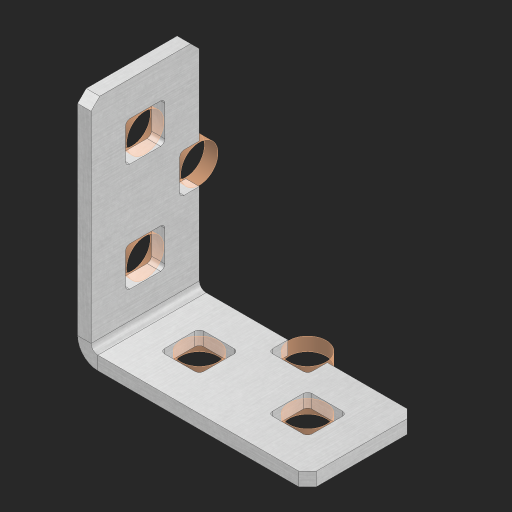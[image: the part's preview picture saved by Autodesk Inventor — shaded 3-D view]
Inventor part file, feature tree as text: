
AUTODESK INVENTOR PART (.ipt)
format: ipt  version: 2023 (Build 270158000, 158)  size: 512,512 bytes
history: native  units: in
note: dims shown in document units (in); Inventor stores cm internally (conversion verified against a paired STEP export)
features: other x78, extrude x70, sheet_metal_op x8, sketch x7, pattern_linear x2, mirror x1, chamfer x1
ambient origin geometry x8: Origin, YZ Plane, XZ Plane, XY Plane, X Axis, Y Axis, Z Axis, Center Point
bodies: Solid1 (feature_tree), Body (feature_tree)
feature tree (167):
  sheet_metal_op  "Flanges"
  sheet_metal_op  "Body Pattern"
  pattern_linear  "Center Pattern"  Spacing1=1.0in  [1 undecoded]
  other  "Arc Length"
  pattern_linear  "Notch Pattern"  Spacing1=0.25in  [1 undecoded]
  other  "Diagonal Plane"
  mirror  "Everything Mirrored"
  chamfer  "End Chamfer"
  sketch  "Sketch1"  dims[d0=1.0in]
  other  "Plate1"
  sketch  "Sketch2"  dims[d1=0.5in]
  other  "Plate2"
  sheet_metal_op  "Bend1"
  sheet_metal_op  "Corner1"
  sketch  "Sketch8"  dims[d2=0.0625in]
  sketch  "Sketch9"  dims[d3=0.0625in]
  other  "Srf91"
  sheet_metal_op  "Body Pattern Sketch"
  other  "Srf92"
  sketch  "Sketch13"  dims[d4=0.0312in]
  sketch  "Sketch15"  dims[d5=0.125in]
  sketch  "Sketch16"  dims[d6=0.0625in d7=1.0in d8=90.0deg d9=0.0312in d10=0.25in d11=0.0625in d12=0.0625in d49=0.182in d50=0.02in d52=0.25in d53=0.0625in d54=0.0in d55=0.172in d56=1.0in d57=0.0in d60=0.3937in d62=0.5in d63=0.7874in d65=0.5in d85=0.1473in d86=0.1782in d89=0.0625in d90=0.0in d91=0.04in d92=0.0491in d95=2.5in d96=0.04in d97=0.25in d98=45.0deg d99=0.25in d106=0.182in d107=0.02in d108=0.5in d110=0.0625in d111=0.0in d112=0.172in d113=0.5in d114=0.0in d117=0.5in d123=0.25in d125=0.25in d126=0.0491in d127=0.1473in d128=0.08in d129=0.04in d130=2.5in]
  other  "Srf786"
  other  "Srf889"
  other  "Srf890"
  other  "Srf891"
  other  "Srf1275"
  other  "Srf1276"
  other  "Srf1277"
  other  "Srf1285"
  other  "Srf1286"
  other  "Srf1287"
  other  "Srf1445"
  other  "Srf1446"
  other  "Srf1447"
  other  "Srf1448"
  other  "Srf1449"
  other  "Srf1450"
  other  "Srf1451"
  other  "Srf1452"
  other  "Srf1453"
  other  "Srf1454"
  other  "Srf1455"
  other  "Srf1456"
  other  "Srf1457"
  other  "Srf1458"
  other  "Srf1459"
  other  "Srf1460"
  other  "Srf1461"
  other  "Srf1462"
  other  "Srf1463"
  other  "Srf1464"
  other  "Srf1465"
  other  "Srf1466"
  other  "Srf1467"
  other  "Srf1468"
  other  "Srf1469"
  other  "Srf1470"
  other  "Srf1471"
  other  "Srf1472"
  other  "Srf1473"
  other  "Srf1474"
  other  "Srf1537"
  other  "Srf1538"
  other  "Srf1539"
  other  "Srf1540"
  other  "Srf1541"
  other  "Srf1542"
  other  "Srf1543"
  other  "Srf1544"
  other  "Srf1545"
  other  "Srf1546"
  other  "Srf1547"
  other  "Srf1548"
  other  "Srf1549"
  other  "Srf1550"
  other  "Srf1551"
  other  "Srf1552"
  other  "Srf1553"
  other  "Srf1554"
  other  "Srf1555"
  other  "Srf1556"
  other  "Srf1557"
  other  "Srf1558"
  other  "Srf1559"
  other  "Srf1560"
  other  "Srf1561"
  other  "Srf1562"
  other  "Srf1563"
  other  "Srf1564"
  other  "Srf1565"
  other  "Srf1566"
  sheet_metal_op  "Body Stamp"
  sheet_metal_op  "Body Circle"
  other  "Center Stamp"
  other  "Center Circle"
  sheet_metal_op  "Notch"
  extrude  "ExtrusionSrf92"  Depth=0.0625in
  extrude  "ExtrusionSrf889"  Depth=0.0625in
  extrude  "ExtrusionSrf890"  Depth=0.182in
  extrude  "ExtrusionSrf891"  Depth=0.02in
  extrude  "ExtrusionSrf1275"  Depth=0.25in
  extrude  "ExtrusionSrf1276"  Depth=0.0625in
  extrude  "ExtrusionSrf1345"  TaperAngle=0.0deg  [1 undecoded]
  extrude  "ExtrusionSrf1346"  Depth=0.25in
  extrude  "ExtrusionSrf1347"  Depth=1.0in TaperAngle=0.0deg
  extrude  "ExtrusionSrf1348"  Depth=0.3937in
  extrude  "ExtrusionSrf1445"  Depth=0.5in
  extrude  "ExtrusionSrf1446"  Depth=0.25in
  extrude  "ExtrusionSrf1447"  Depth=0.25in
  extrude  "ExtrusionSrf1448"  Depth=0.0625in
  extrude  "ExtrusionSrf1449"  Depth=0.25in TaperAngle=0.0deg
  extrude  "ExtrusionSrf1450"  Depth=0.25in
  extrude  "ExtrusionSrf1451"  Depth=0.25in TaperAngle=45.0deg
  extrude  "ExtrusionSrf1452"  Depth=0.25in
  extrude  "ExtrusionSrf1453"  Depth=0.182in
  extrude  "ExtrusionSrf1454"  Depth=0.02in
  extrude  "ExtrusionSrf1455"  Depth=0.5in
  extrude  "ExtrusionSrf1456"  Depth=0.0625in
  extrude  "ExtrusionSrf1457"  TaperAngle=0.0deg  [1 undecoded]
  extrude  "ExtrusionSrf1458"  Depth=0.25in
  extrude  "ExtrusionSrf1459"  Depth=0.5in TaperAngle=0.0deg
  extrude  "ExtrusionSrf1460"  Depth=0.5in
  extrude  "ExtrusionSrf1461"  Depth=0.25in
  extrude  "ExtrusionSrf1462"  Depth=0.25in
  extrude  "ExtrusionSrf1463"  Depth=0.25in
  extrude  "ExtrusionSrf1464"  Depth=0.25in
  extrude  "ExtrusionSrf1465"  Depth=0.25in
  extrude  "ExtrusionSrf1466"  Depth=0.25in
  extrude  "ExtrusionSrf1467"  Depth=0.25in
  extrude  "ExtrusionSrf1468"  [1 undecoded]
  extrude  "ExtrusionSrf1469"  [1 undecoded]
  extrude  "ExtrusionSrf1470"  [1 undecoded]
  extrude  "ExtrusionSrf1471"  [1 undecoded]
  extrude  "ExtrusionSrf1472"  [1 undecoded]
  extrude  "ExtrusionSrf1473"  [1 undecoded]
  extrude  "ExtrusionSrf1474"  [1 undecoded]
  extrude  "ExtrusionSrf1537"  [1 undecoded]
  extrude  "ExtrusionSrf1538"  [1 undecoded]
  extrude  "ExtrusionSrf1539"  [1 undecoded]
  extrude  "ExtrusionSrf1540"  [1 undecoded]
  extrude  "ExtrusionSrf1541"  [1 undecoded]
  extrude  "ExtrusionSrf1542"  [1 undecoded]
  extrude  "ExtrusionSrf1543"  [1 undecoded]
  extrude  "ExtrusionSrf1544"  [1 undecoded]
  extrude  "ExtrusionSrf1545"  [1 undecoded]
  extrude  "ExtrusionSrf1546"  [1 undecoded]
  extrude  "ExtrusionSrf1547"  [1 undecoded]
  extrude  "ExtrusionSrf1548"  [1 undecoded]
  extrude  "ExtrusionSrf1549"  [1 undecoded]
  extrude  "ExtrusionSrf1550"  [1 undecoded]
  extrude  "ExtrusionSrf1551"  [1 undecoded]
  extrude  "ExtrusionSrf1552"  [1 undecoded]
  extrude  "ExtrusionSrf1553"  [1 undecoded]
  extrude  "ExtrusionSrf1554"  [1 undecoded]
  extrude  "ExtrusionSrf1555"  [1 undecoded]
  extrude  "ExtrusionSrf1556"  [1 undecoded]
  extrude  "ExtrusionSrf1557"  [1 undecoded]
  extrude  "ExtrusionSrf1558"  [1 undecoded]
  extrude  "ExtrusionSrf1559"  [1 undecoded]
  extrude  "ExtrusionSrf1560"  [1 undecoded]
  extrude  "ExtrusionSrf1561"  [1 undecoded]
  extrude  "ExtrusionSrf1562"  [1 undecoded]
  extrude  "ExtrusionSrf1563"  [1 undecoded]
  extrude  "ExtrusionSrf1564"  [1 undecoded]
  extrude  "ExtrusionSrf1565"  [1 undecoded]
  extrude  "ExtrusionSrf1566"  [1 undecoded]
note: 41 required parameter values undecoded (feature->parameter linkage not recoverable at this tier; creation-order binding heuristic only, values carry confidence <= 0.55)
